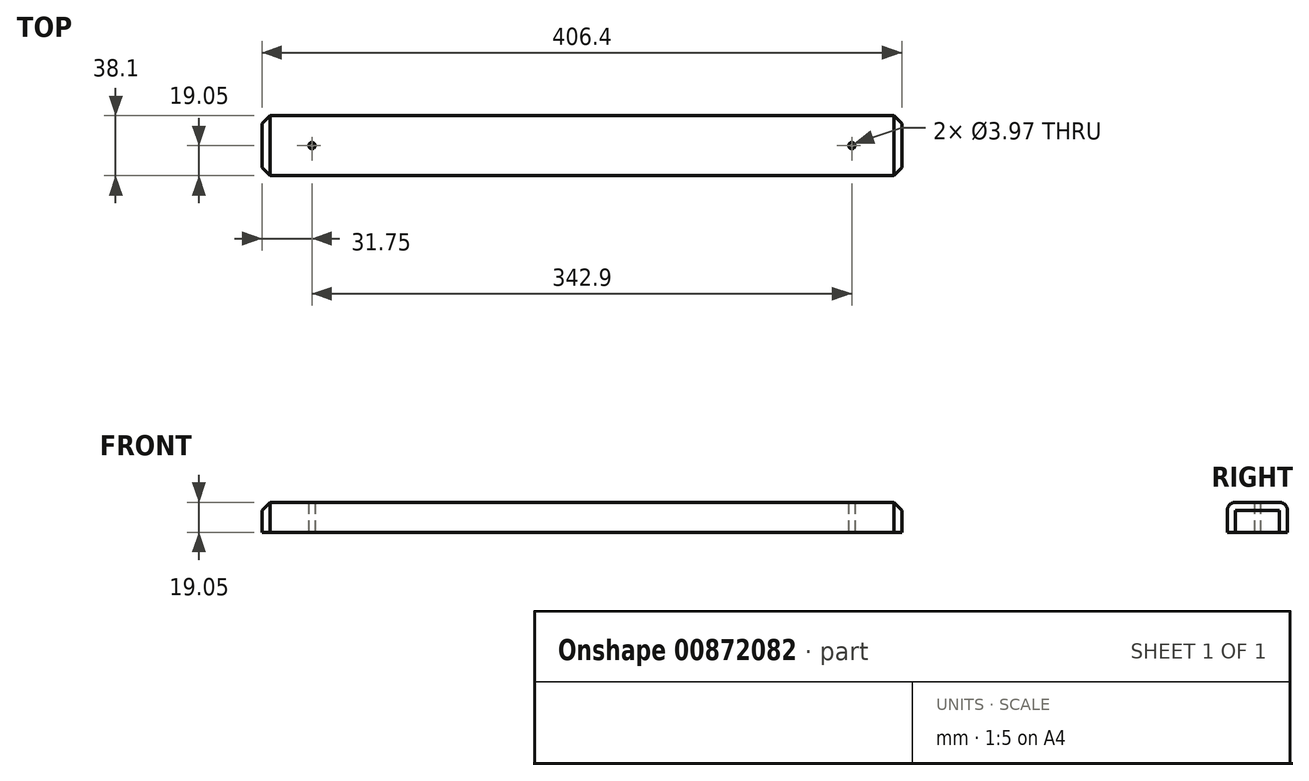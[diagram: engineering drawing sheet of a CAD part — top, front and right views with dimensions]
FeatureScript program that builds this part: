
annotation { "Feature Type Name" : "Feature", "Feature Type Description" : "" }
export const myFeature = defineFeature(function(context is Context, id is Id, definition is map)
    precondition{}
    {
        {
            var Q0;
            Q0=qCreatedBy(makeId("Right.planeOp"),FACE);
            var sketch = newSketch(context, id + "F0", { "sketchPlane" : qUnion([Q0])});
            skLineSegment(sketch, "E0.bottom", {"start": v(0, 0) * mm, "end": v(38.1, 0) * mm});
            skLineSegment(sketch, "E0.top", {"start": v(0, 19.05) * mm, "end": v(38.1, 19.05) * mm});
            skLineSegment(sketch, "E0.left", {"start": v(0, 0) * mm, "end": v(0, 19.05) * mm});
            skLineSegment(sketch, "E0.right", {"start": v(38.1, 0) * mm, "end": v(38.1, 19.05) * mm});
            skSolve(sketch);
        }
        {
            var Q0;
            Q0=qSketchRegion(id+"F0",true);
            extrude(context, id + "F1", {"entities" : qUnion([Q0]), "depth" : 406.4 * mm});
        }
        {
            var Q0;
            Q0=makeQuery(id+"F1.opExtrude","SWEPT_EDGE",EDGE,{"disambiguationData":[OSD([sQuery(id+"F0.wireOp",EDGE,"E0.top"),sQuery(id+"F0.wireOp",EDGE,"E0.left")])]});
            var Q1;
            Q1=makeQuery(id+"F1.opExtrude","SWEPT_EDGE",EDGE,{"disambiguationData":[OSD([sQuery(id+"F0.wireOp",EDGE,"E0.top"),sQuery(id+"F0.wireOp",EDGE,"E0.right")])]});
            fillet(context, id + "F2", {"entities" : qUnion([Q0, Q1]), "radius" : 5.08 * mm, "tangentPropagation" : true, "allowEdgeOverflow" : false});
        }
        {
            var Q0;
            Q0=makeQuery(id+"F1.opExtrude","CAP_EDGE",EDGE,{"disambiguationData":[OSD([sQuery(id+"F0.wireOp",EDGE,"E0.top")])],"isStart":false});
            var Q1;
            Q1=makeQuery(id+"F1.opExtrude","CAP_EDGE",EDGE,{"disambiguationData":[OSD([sQuery(id+"F0.wireOp",EDGE,"E0.top")])],"isStart":true});
            chamfer(context, id + "F3", {"entities" : qUnion([Q0, Q1]), "width" : 5.08 * mm, "tangentPropagation" : true});
        }
        {
            var Q0;
            Q0=makeQuery(id+"F1.opExtrude","SWEPT_FACE",FACE,{"disambiguationData":[OSD([sQuery(id+"F0.wireOp",EDGE,"E0.bottom")])]});
            var sketch = newSketch(context, id + "F4", { "sketchPlane" : qUnion([Q0])});
            skCircle(sketch, "E1", {"center": v(31.75, -19.05) * mm, "radius": 1.98 * mm});
            skLineSegment(sketch, "E2", {"start": v(203.2, 12.96) * mm, "end": v(203.2, -63.34) * mm, "construction": true});
            skPoint(sketch, "E2.startSnap0", {"position": v(203.2, 0) * mm});
            skCircle(sketch, "E3.MirrorC", {"center": v(374.65, -19.05) * mm, "radius": 1.98 * mm});
            skSolve(sketch);
        }
        {
            var Q0;
            Q0=qSketchRegion(id+"F4",true);
            extrude(context, id + "F5", {"entities" : qUnion([Q0]), "operationType" : NewBodyOperationType.REMOVE, "oppositeDirection" : true, "depth" : 25.4 * mm});
        }
    });
